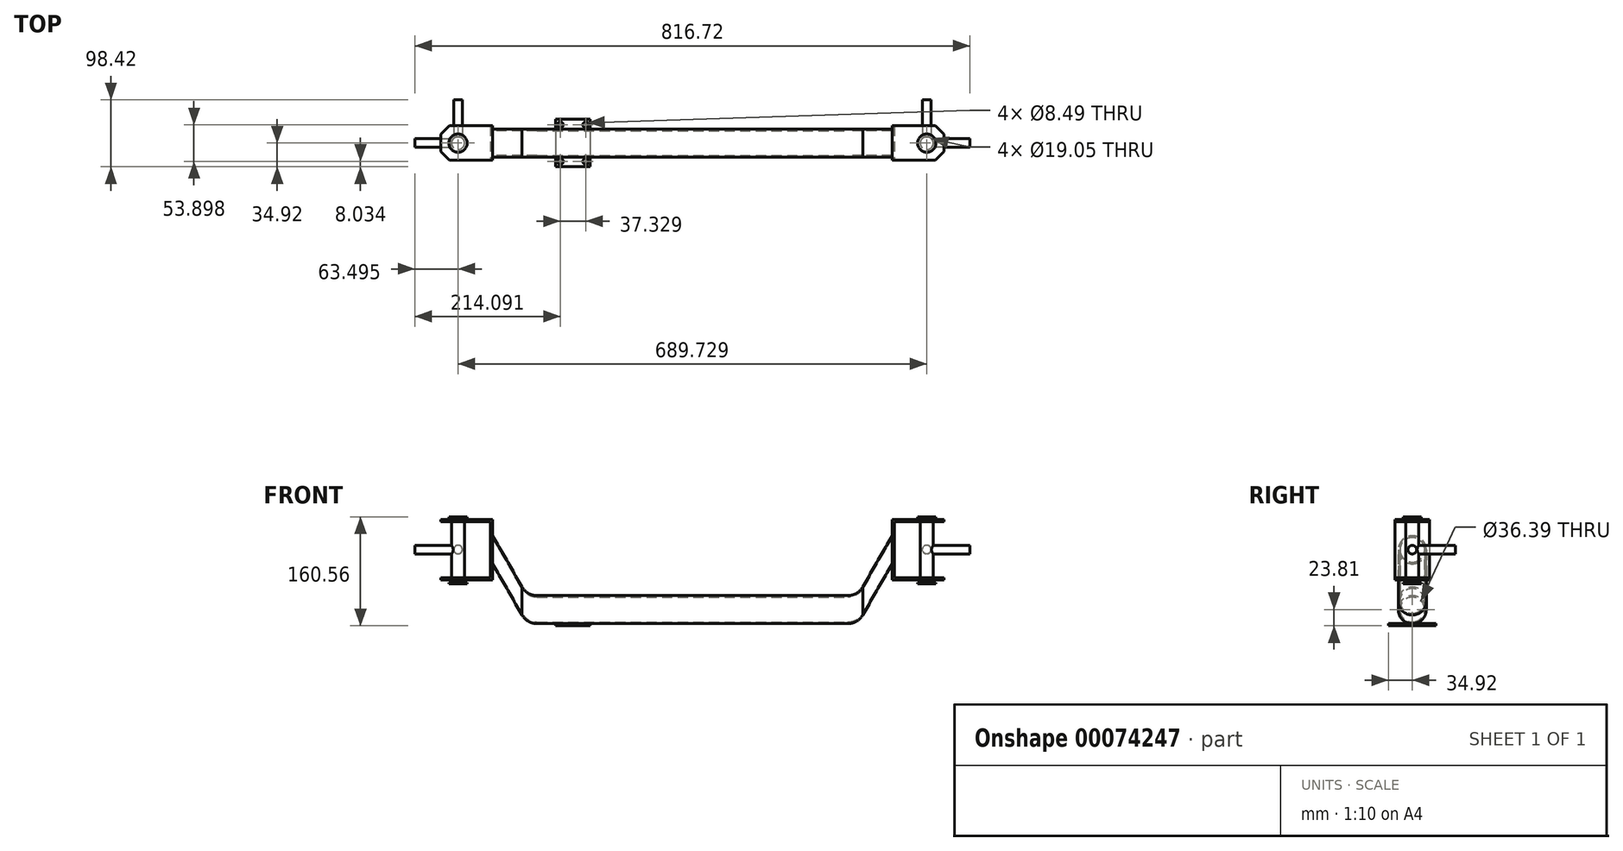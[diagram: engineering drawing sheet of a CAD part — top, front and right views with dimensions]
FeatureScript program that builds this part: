
annotation { "Feature Type Name" : "Feature", "Feature Type Description" : "" }
export const myFeature = defineFeature(function(context is Context, id is Id, definition is map)
    precondition{}
    {
        {
            var Q0;
            Q0=qCreatedBy(makeId("Front.planeOp"),FACE);
            var sketch = newSketch(context, id + "F0", { "sketchPlane" : qUnion([Q0])});
            skLineSegment(sketch, "E0", {"start": v(-228.6, 0) * mm, "end": v(228.6, 0) * mm});
            skLineSegment(sketch, "E1", {"start": v(250.6, 12.7) * mm, "end": v(294.06, 87.99) * mm});
            skLineSegment(sketch, "E2", {"start": v(-250.6, 12.7) * mm, "end": v(-294.06, 87.99) * mm});
            skPoint(sketch, "E3", {"position": v(-294.06, 87.99) * mm});
            skPoint(sketch, "E4", {"position": v(294.06, 87.99) * mm});
            skPoint(sketch, "E5", {"position": v(0, 0) * mm});
            skPoint(sketch, "E6.visualSharp", {"position": v(-243.26, 0) * mm});
            skArc(sketch, "E6.filletArc", {"start": v(-250.6, 12.7) * mm, "mid": v(-241.3, 3.4) * mm, "end": v(-228.6, 0) * mm});
            skPoint(sketch, "E7.visualSharp", {"position": v(243.26, 0) * mm});
            skArc(sketch, "E7.filletArc", {"start": v(228.6, 0) * mm, "mid": v(241.3, 3.4) * mm, "end": v(250.6, 12.7) * mm});
            skSolve(sketch);
        }
        {
            var Q0;
            Q0=qCreatedBy(makeId("Right.planeOp"),FACE);
            var Q1;
            Q1=sQuery(id+"F0.wireOp",VERTEX,"E3");
            var Q2;
            Q2 = qBodyType(qCreatedBy(id + "F2" ,EDGE), BodyType.WIRE);
            cPlane(context, id + "F1", {"entities" : qUnion([Q0, Q1, Q2]), "cplaneType" : CPlaneType.PLANE_POINT, "offset" : 152.4 * mm, "width" : 152.4 * mm, "height" : 152.4 * mm});
        }
        {
            var Q0;
            Q0=qCreatedBy(id+"F1.planeOp",FACE);
            var sketch = newSketch(context, id + "F2", { "sketchPlane" : qUnion([Q0])});
            skCircle(sketch, "E8", {"center": v(0, 87.99) * mm, "radius": 20.64 * mm});
            skCircle(sketch, "E9", {"center": v(0, 87.99) * mm, "radius": 18.2 * mm});
            skSolve(sketch);
        }
        {
            var Q0;
            Q0=makeQuery(id+"F2.imprint","IMPRINT",FACE,{"disambiguationData":[TD([[makeQuery(id+"F2.imprint","IMPRINT",EDGE,{"derivedFrom":sQuery(id+"F2.wireOp",EDGE,"E8")}),1.0]])]});
            var Q1;
            Q1 = qSketchRegion(id + "F0", true);
            var Q2;
            Q2=sQuery(id+"F0.wireOp",EDGE,"E2");
            var Q3;
            Q3=sQuery(id+"F0.wireOp",EDGE,"E6.filletArc");
            var Q4;
            Q4=sQuery(id+"F0.wireOp",EDGE,"E0");
            var Q5;
            Q5=sQuery(id+"F0.wireOp",EDGE,"E7.filletArc");
            var Q6;
            Q6=sQuery(id+"F0.wireOp",EDGE,"E1");
            sweep(context, id + "F3", {"profiles" : qUnion([Q0, Q1]), "path" : qUnion([Q2, Q3, Q4, Q5, Q6]), "keepProfileOrientation" : true});
        }
        {
            var Q0;
            Q0=qCreatedBy(id+"F1.planeOp",FACE);
            var sketch = newSketch(context, id + "F4", { "sketchPlane" : qUnion([Q0])});
            skCircle(sketch, "E10.0", {"center": v(0, 87.99) * mm, "radius": 18.2 * mm});
            skLineSegment(sketch, "E11.bottom", {"start": v(25.4, 132.54) * mm, "end": v(-25.4, 132.54) * mm});
            skLineSegment(sketch, "E11.top", {"start": v(25.4, 43.44) * mm, "end": v(-25.4, 43.44) * mm});
            skLineSegment(sketch, "E11.left", {"start": v(25.4, 132.54) * mm, "end": v(25.4, 43.44) * mm});
            skLineSegment(sketch, "E11.right", {"start": v(-25.4, 132.54) * mm, "end": v(-25.4, 43.44) * mm});
            skLineSegment(sketch, "E12", {"start": v(25.4, 129.36) * mm, "end": v(-25.4, 129.36) * mm});
            skLineSegment(sketch, "E13", {"start": v(25.4, 46.61) * mm, "end": v(-25.4, 46.61) * mm});
            skSolve(sketch);
        }
        {
            var Q0;
            Q0=makeQuery(id+"F4.imprint","IMPRINT",FACE,{"disambiguationData":[TD([[makeQuery(id+"F4.imprint","IMPRINT",EDGE,{"derivedFrom":sQuery(id+"F4.wireOp",EDGE,"E10.0")}),-1.0]])]});
            var Q1;
            Q1=makeQuery(id+"F4.imprint","IMPRINT",FACE,{"disambiguationData":[TD([[makeQuery(id+"F4.imprint","IMPRINT",EDGE,{"derivedFrom":sQuery(id+"F4.wireOp",EDGE,"E10.0")}),1.0]])]});
            extrude(context, id + "F5", {"entities" : qUnion([Q0, Q1]), "oppositeDirection" : true, "depth" : 3.17 * mm});
        }
        {
            var Q0;
            {var subQ0=sQuery(id+"F4.wireOp",EDGE,"E11.bottom");Q0=makeQuery(id+"F4.imprint","IMPRINT",FACE,{"disambiguationData":[TD([[makeQuery(id+"F4.imprint","IMPRINT",EDGE,{"derivedFrom":subQ0}),1.0]])]});}
            var Q1;
            {var subQ0=sQuery(id+"F4.wireOp",EDGE,"E11.top");Q1=makeQuery(id+"F4.imprint","IMPRINT",FACE,{"disambiguationData":[TD([[makeQuery(id+"F4.imprint","IMPRINT",EDGE,{"derivedFrom":subQ0}),-1.0]])]});}
            extrude(context, id + "F6", {"entities" : qUnion([Q0, Q1]), "operationType" : NewBodyOperationType.ADD, "oppositeDirection" : true, "depth" : 76.2 * mm});
        }
        {
            var Q0;
            Q0=makeQuery(id+"F6.opExtrude","SWEPT_FACE",FACE,{"disambiguationData":[OSD([sQuery(id+"F4.wireOp",EDGE,"E11.bottom")])]});
            var sketch = newSketch(context, id + "F7", { "sketchPlane" : qUnion([Q0])});
            skLineSegment(sketch, "E14.0", {"start": v(-370.26, 25.4) * mm, "end": v(-294.06, 25.4) * mm});
            skLineSegment(sketch, "E15.0", {"start": v(-370.26, 25.4) * mm, "end": v(-370.26, -25.4) * mm});
            skLineSegment(sketch, "E16.0", {"start": v(-370.26, -25.4) * mm, "end": v(-294.06, -25.4) * mm});
            skCircle(sketch, "E17", {"center": v(-344.86, 0) * mm, "radius": 9.53 * mm});
            skPoint(sketch, "E17.centerSnap0", {"position": v(-370.26, 0) * mm});
            skPoint(sketch, "E17.centerSnap1", {"position": v(-344.86, 25.4) * mm});
            skSolve(sketch);
        }
        {
            var Q0;
            Q0=makeQuery(id+"F7.imprint","IMPRINT",FACE,{"disambiguationData":[TD([[makeQuery(id+"F7.imprint","IMPRINT",EDGE,{"derivedFrom":sQuery(id+"F7.wireOp",EDGE,"E17")}),1.0]])]});
            extrude(context, id + "F8", {"entities" : qUnion([Q0]), "operationType" : NewBodyOperationType.REMOVE, "endBound" : BoundingType.THROUGH_ALL, "oppositeDirection" : true, "depth" : 25.4 * mm});
        }
        {
            var Q0;
            {var subQ0=sQuery(id+"F4.wireOp",EDGE,"E11.right");Q0=makeQuery(id+"F6.opExtrude","CAP_EDGE",EDGE,{"disambiguationData":[OSD([subQ0]),TDD([makeQuery(id+"F4.imprint","IMPRINT",EDGE,{"disambiguationData":[TD([[makeQuery(id+"F4.imprint","INTERSECT",VERTEX,{"derivedFrom":[sQuery(id+"F4.wireOp",EDGE,"E11.bottom"),subQ0]}),-1.0]])],"derivedFrom":subQ0})])],"isStart":false});}
            var Q1;
            {var subQ0=sQuery(id+"F4.wireOp",EDGE,"E11.left");Q1=makeQuery(id+"F6.opExtrude","CAP_EDGE",EDGE,{"disambiguationData":[OSD([subQ0]),TDD([makeQuery(id+"F4.imprint","IMPRINT",EDGE,{"disambiguationData":[TD([[makeQuery(id+"F4.imprint","INTERSECT",VERTEX,{"derivedFrom":[sQuery(id+"F4.wireOp",EDGE,"E11.bottom"),subQ0]}),-1.0]])],"derivedFrom":subQ0})])],"isStart":false});}
            var Q2;
            {var subQ0=sQuery(id+"F4.wireOp",EDGE,"E11.right");Q2=makeQuery(id+"F6.opExtrude","CAP_EDGE",EDGE,{"disambiguationData":[OSD([subQ0]),TDD([makeQuery(id+"F4.imprint","IMPRINT",EDGE,{"disambiguationData":[TD([[makeQuery(id+"F4.imprint","INTERSECT",VERTEX,{"derivedFrom":[sQuery(id+"F4.wireOp",EDGE,"E11.top"),subQ0]}),1.0]])],"derivedFrom":subQ0})])],"isStart":false});}
            var Q3;
            {var subQ0=sQuery(id+"F4.wireOp",EDGE,"E11.left");Q3=makeQuery(id+"F6.opExtrude","CAP_EDGE",EDGE,{"disambiguationData":[OSD([subQ0]),TDD([makeQuery(id+"F4.imprint","IMPRINT",EDGE,{"disambiguationData":[TD([[makeQuery(id+"F4.imprint","INTERSECT",VERTEX,{"derivedFrom":[sQuery(id+"F4.wireOp",EDGE,"E11.top"),subQ0]}),1.0]])],"derivedFrom":subQ0})])],"isStart":false});}
            chamfer(context, id + "F9", {"entities" : qUnion([Q0, Q1, Q2, Q3]), "width" : 12.7 * mm});
        }
        {
            var Q0;
            Q0=qCreatedBy(id+"F1.planeOp",FACE);
            cPlane(context, id + "F10", {"entities" : qUnion([Q0]), "cplaneType" : CPlaneType.OFFSET, "offset" : 25.4 * mm, "oppositeDirection" : true, "width" : 152.4 * mm, "height" : 152.4 * mm});
        }
        {
            var Q0;
            Q0=qCreatedBy(makeId("Top.planeOp"),FACE);
            cPlane(context, id + "F11", {"entities" : qUnion([Q0]), "cplaneType" : CPlaneType.OFFSET, "offset" : 20.64 * mm, "oppositeDirection" : true, "width" : 152.4 * mm, "height" : 152.4 * mm});
        }
        {
            var Q0;
            Q0=qCreatedBy(id+"F11.planeOp",FACE);
            var sketch = newSketch(context, id + "F12", { "sketchPlane" : qUnion([Q0])});
            skLineSegment(sketch, "E18.bottom", {"start": v(-201.11, 34.93) * mm, "end": v(-150.31, 34.93) * mm});
            skLineSegment(sketch, "E18.top", {"start": v(-201.11, -34.93) * mm, "end": v(-150.31, -34.93) * mm});
            skLineSegment(sketch, "E18.left", {"start": v(-201.11, 34.93) * mm, "end": v(-201.11, -34.93) * mm});
            skLineSegment(sketch, "E18.right", {"start": v(-150.31, 34.93) * mm, "end": v(-150.31, -34.93) * mm});
            skPoint(sketch, "E18.middle", {"position": v(-175.71, 0) * mm});
            skCircle(sketch, "E19", {"center": v(-194.27, 27.01) * mm, "radius": 4.24 * mm});
            skCircle(sketch, "E20.0.1.0", {"center": v(-194.27, -26.89) * mm, "radius": 4.24 * mm});
            skCircle(sketch, "E20.1.0.0", {"center": v(-156.94, 27.01) * mm, "radius": 4.24 * mm});
            skCircle(sketch, "E20.1.1.0", {"center": v(-156.94, -26.89) * mm, "radius": 4.24 * mm});
            skLineSegment(sketch, "E20.direction1", {"start": v(-194.27, 27.01) * mm, "end": v(-156.94, 27.01) * mm, "construction": true});
            skLineSegment(sketch, "E20.direction2", {"start": v(-194.27, 27.01) * mm, "end": v(-194.27, -26.89) * mm, "construction": true});
            skSolve(sketch);
        }
        {
            var Q0;
            Q0 = qSketchRegion(id + "F12", true);
            extrude(context, id + "F13", {"entities" : qUnion([Q0]), "oppositeDirection" : true, "depth" : 3.17 * mm});
        }
        {
            var Q0;
            Q0=makeQuery(id+"F6.opExtrude","SWEPT_BODY",BODY,{"disambiguationData":[OSD([sQuery(id+"F4.wireOp",EDGE,"E11.bottom"),sQuery(id+"F4.wireOp",EDGE,"E11.left"),sQuery(id+"F4.wireOp",EDGE,"E11.right"),sQuery(id+"F4.wireOp",EDGE,"E12")])]});
            var Q1;
            Q1=makeQuery(id+"F6.opExtrude","SWEPT_BODY",BODY,{"disambiguationData":[OSD([sQuery(id+"F4.wireOp",EDGE,"E11.top"),sQuery(id+"F4.wireOp",EDGE,"E11.left"),sQuery(id+"F4.wireOp",EDGE,"E11.right"),sQuery(id+"F4.wireOp",EDGE,"E13")])]});
            var Q2;
            Q2=makeQuery(id+"F5.opExtrude","SWEPT_BODY",BODY,{"disambiguationData":[OSD([sQuery(id+"F4.wireOp",EDGE,"E11.left"),sQuery(id+"F4.wireOp",EDGE,"E11.right"),sQuery(id+"F4.wireOp",EDGE,"E12"),sQuery(id+"F4.wireOp",EDGE,"E13")])]});
            var Q3;
            Q3=qCreatedBy(makeId("Right.planeOp"),FACE);
            mirror(context, id + "F14", {"operationType" : NewBodyOperationType.ADD, "entities" : qUnion([Q0, Q1, Q2]), "mirrorPlane" : qUnion([Q3])});
        }
        {
            var Q0;
            Q0=makeQuery(id+"F6.opExtrude","SWEPT_FACE",FACE,{"disambiguationData":[OSD([sQuery(id+"F4.wireOp",EDGE,"E11.top")])]});
            var sketch = newSketch(context, id + "F15", { "sketchPlane" : qUnion([Q0])});
            skCircle(sketch, "E21.0", {"center": v(-344.86, 0) * mm, "radius": 9.53 * mm});
            skSolve(sketch);
        }
        {
            var Q0;
            Q0 = qSketchRegion(id + "F15", true);
            extrude(context, id + "F16", {"entities" : qUnion([Q0]), "oppositeDirection" : true, "depth" : 91.8 * mm, "hasSecondDirection" : true, "secondDirectionOppositeDirection" : false, "secondDirectionDepth" : 3.23 * mm});
        }
        {
            var Q0;
            Q0=makeQuery(id+"F16.opExtrude","CAP_FACE",FACE,{"disambiguationData":[OSD([sQuery(id+"F15.wireOp",EDGE,"E21.0")])],"isStart":true});
            var sketch = newSketch(context, id + "F17", { "sketchPlane" : qUnion([Q0])});
            skCircle(sketch, "E22", {"center": v(-344.86, 0) * mm, "radius": 13.44 * mm});
            skSolve(sketch);
        }
        {
            var Q0;
            Q0 = qSketchRegion(id + "F17", true);
            extrude(context, id + "F18", {"entities" : qUnion([Q0]), "operationType" : NewBodyOperationType.ADD, "depth" : 2.04 * mm});
        }
        {
            var Q0;
            Q0=makeQuery(id+"F16.opExtrude","CAP_FACE",FACE,{"disambiguationData":[OSD([sQuery(id+"F15.wireOp",EDGE,"E21.0")])],"isStart":false});
            var sketch = newSketch(context, id + "F19", { "sketchPlane" : qUnion([Q0])});
            skCircle(sketch, "E23", {"center": v(-344.86, 0) * mm, "radius": 13.42 * mm});
            skSolve(sketch);
        }
        {
            var Q0;
            Q0 = qSketchRegion(id + "F19", true);
            extrude(context, id + "F20", {"entities" : qUnion([Q0]), "operationType" : NewBodyOperationType.ADD, "depth" : 1.5 * mm});
        }
        {
            var Q0;
            Q0=qCreatedBy(id+"F10.planeOp",FACE);
            var Q1;
            Q1=makeQuery(id+"F16.opExtrude","SWEPT_FACE",FACE,{"disambiguationData":[OSD([sQuery(id+"F15.wireOp",EDGE,"E21.0")])]});
            cPlane(context, id + "F21", {"entities" : qUnion([Q0, Q1]), "cplaneType" : CPlaneType.LINE_ANGLE, "offset" : 152.4 * mm, "angle" : 0 * degree, "width" : 152.4 * mm, "height" : 152.4 * mm});
        }
        {
            var Q0;
            {var subQ0=sQuery(id+"F4.wireOp",EDGE,"E11.left");Q0=makeQuery(id+"F14.boolean.opBoolean","MERGE",FACE,{"derivedFrom":[makeQuery(id+"F5.opExtrude","SWEPT_FACE",FACE,{"disambiguationData":[OSD([subQ0])]}),makeQuery(id+"F6.opExtrude","SWEPT_FACE",FACE,{"disambiguationData":[OSD([subQ0]),TDD([makeQuery(id+"F4.imprint","IMPRINT",EDGE,{"disambiguationData":[TD([[makeQuery(id+"F4.imprint","INTERSECT",VERTEX,{"derivedFrom":[sQuery(id+"F4.wireOp",EDGE,"E11.bottom"),subQ0]}),-1.0]])],"derivedFrom":subQ0})])]}),makeQuery(id+"F6.opExtrude","SWEPT_FACE",FACE,{"disambiguationData":[OSD([subQ0]),TDD([makeQuery(id+"F4.imprint","IMPRINT",EDGE,{"disambiguationData":[TD([[makeQuery(id+"F4.imprint","INTERSECT",VERTEX,{"derivedFrom":[sQuery(id+"F4.wireOp",EDGE,"E11.top"),subQ0]}),1.0]])],"derivedFrom":subQ0})])]})]});}
            var Q1;
            Q1=makeQuery(id+"F16.opExtrude","SWEPT_FACE",FACE,{"disambiguationData":[OSD([sQuery(id+"F15.wireOp",EDGE,"E21.0")])]});
            cPlane(context, id + "F22", {"entities" : qUnion([Q0, Q1]), "cplaneType" : CPlaneType.LINE_ANGLE, "offset" : 152.4 * mm, "angle" : 0 * degree, "width" : 152.4 * mm, "height" : 152.4 * mm});
        }
        {
            var Q0;
            Q0=qCreatedBy(id+"F21.planeOp",FACE);
            var sketch = newSketch(context, id + "F23", { "sketchPlane" : qUnion([Q0])});
            skCircle(sketch, "E24", {"center": v(0, 88.22) * mm, "radius": 6.35 * mm});
            skSolve(sketch);
        }
        {
            var Q0;
            Q0 = qSketchRegion(id + "F23", true);
            extrude(context, id + "F24", {"entities" : qUnion([Q0]), "operationType" : NewBodyOperationType.ADD, "depth" : 63.5 * mm});
        }
        {
            var Q0;
            Q0=qCreatedBy(id+"F22.planeOp",FACE);
            var sketch = newSketch(context, id + "F25", { "sketchPlane" : qUnion([Q0])});
            skCircle(sketch, "E25", {"center": v(-344.82, 88.47) * mm, "radius": 6.35 * mm});
            skSolve(sketch);
        }
        {
            var Q0;
            Q0 = qSketchRegion(id + "F25", true);
            extrude(context, id + "F26", {"entities" : qUnion([Q0]), "operationType" : NewBodyOperationType.ADD, "oppositeDirection" : true, "depth" : 63.5 * mm});
        }
        {
            var Q0;
            Q0=makeQuery(id+"F16.opExtrude","SWEPT_BODY",BODY,{"disambiguationData":[OSD([sQuery(id+"F15.wireOp",EDGE,"E21.0")])]});
            var Q1;
            Q1=qCreatedBy(makeId("Right.planeOp"),FACE);
            mirror(context, id + "F27", {"entities" : qUnion([Q0]), "mirrorPlane" : qUnion([Q1])});
        }
    });
